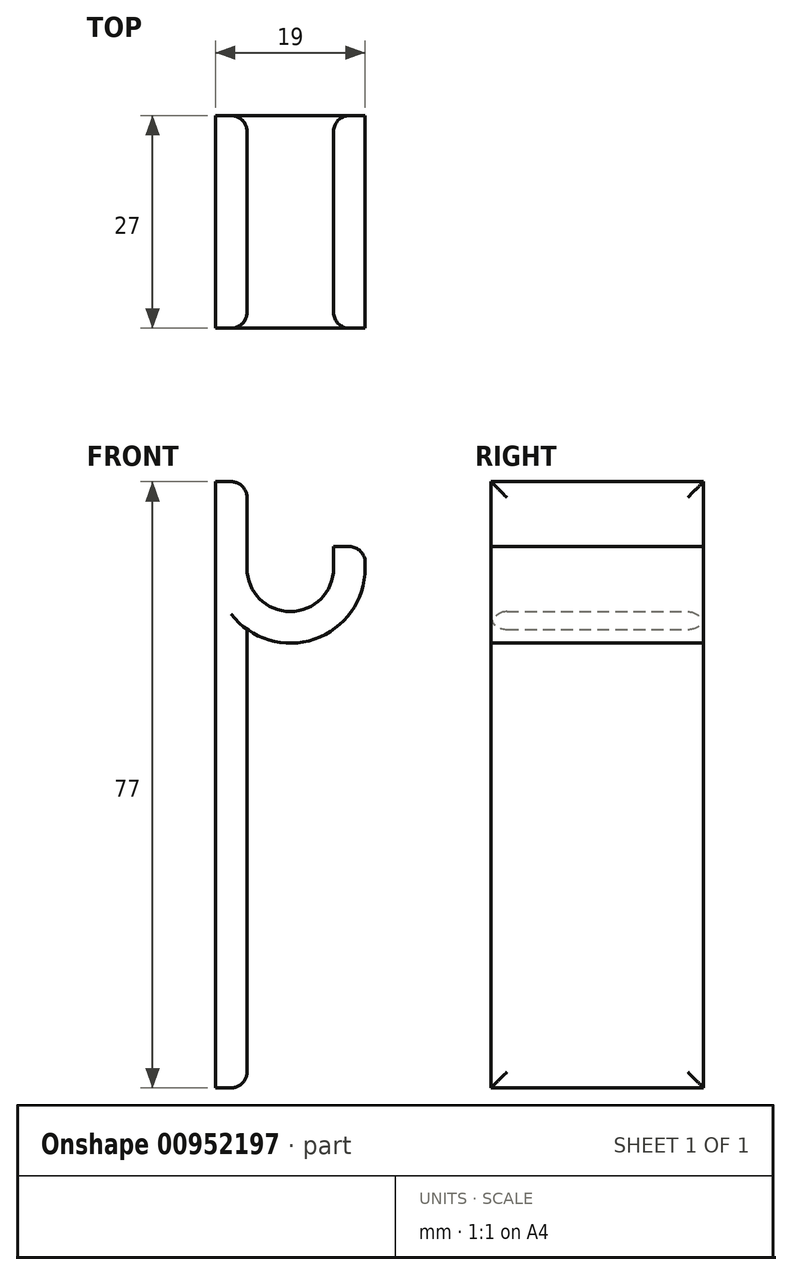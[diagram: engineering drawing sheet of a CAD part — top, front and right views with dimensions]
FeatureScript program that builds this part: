
annotation { "Feature Type Name" : "Feature", "Feature Type Description" : "" }
export const myFeature = defineFeature(function(context is Context, id is Id, definition is map)
    precondition{}
    {
        {
            assignVariable(context, id + "F0", {"name" : "stripWidth", "anyValue" : 27});
        }
        {
            var Q0;
            Q0=qCreatedBy(makeId("Front.planeOp"),FACE);
            var sketch = newSketch(context, id + "F1", { "sketchPlane" : qUnion([Q0])});
            skLineSegment(sketch, "E0.bottom", {"start": v(0, 16.5) * mm, "end": v(4, 16.5) * mm});
            skLineSegment(sketch, "E0.top", {"start": v(0, -60.5) * mm, "end": v(4, -60.5) * mm});
            skLineSegment(sketch, "E0.left", {"start": v(0, 16.5) * mm, "end": v(0, -60.5) * mm});
            skLineSegment(sketch, "E0.right", {"start": v(4, 16.5) * mm, "end": v(4, -60.5) * mm});
            skLineSegment(sketch, "E1", {"start": v(-22.13, 0) * mm, "end": v(36.5, 0) * mm});
            skArc(sketch, "E2", {"start": v(4, 5.5) * mm, "mid": v(9.5, 0) * mm, "end": v(15, 5.5) * mm});
            skArc(sketch, "E3", {"start": v(4, 13.25) * mm, "mid": v(5.14, -2.94) * mm, "end": v(19, 5.5) * mm});
            skLineSegment(sketch, "E4", {"start": v(0, 5.5) * mm, "end": v(4, 5.5) * mm});
            skLineSegment(sketch, "E5.trimOffspring", {"start": v(15, 5.5) * mm, "end": v(19, 5.5) * mm});
            skLineSegment(sketch, "E6.top", {"start": v(15, 8.25) * mm, "end": v(19, 8.25) * mm});
            skLineSegment(sketch, "E6.left", {"start": v(15, 5.5) * mm, "end": v(15, 8.25) * mm});
            skLineSegment(sketch, "E6.right", {"start": v(19, 5.5) * mm, "end": v(19, 8.25) * mm});
            skSolve(sketch);
        }
        {
            var Q0;
            Q0=qSketchRegion(id+"F1",true);
            extrude(context, id + "F2", {"entities" : qUnion([Q0]), "depth" : (getVariable(context, 'stripWidth')) * mm, "offsetDistance" : 25 * mm});
        }
        {
            var Q0;
            {var subQ0=sQuery(id+"F1.wireOp",EDGE,"E0.right");Q0=makeQuery(id+"F2.opExtrude","CAP_EDGE",EDGE,{"disambiguationData":[OSD([subQ0]),TDD([makeQuery(id+"F1.imprint","IMPRINT",EDGE,{"disambiguationData":[TD([[makeQuery(id+"F1.imprint","INTERSECT",VERTEX,{"derivedFrom":[sQuery(id+"F1.wireOp",EDGE,"E0.top"),subQ0]}),1.0]])],"derivedFrom":subQ0})])],"isStart":false});}
            var Q1;
            {var subQ0=sQuery(id+"F1.wireOp",EDGE,"E0.right");var subQ1=makeQuery(id+"F1.imprint","INTERSECT",VERTEX,{"disambiguationData":[OD(0.0)],"derivedFrom":[subQ0,sQuery(id+"F1.wireOp",EDGE,"E3")]});Q1=makeQuery(id+"F2.opExtrude","CAP_EDGE",EDGE,{"disambiguationData":[OSD([subQ0]),TDD([makeQuery(id+"F1.imprint","IMPRINT",EDGE,{"disambiguationData":[TD([[makeQuery(id+"F1.imprint","INTERSECT",VERTEX,{"derivedFrom":[sQuery(id+"F1.wireOp",EDGE,"E0.bottom"),subQ0]}),-1.0]])],"derivedFrom":subQ0}),makeQuery(id+"F1.imprint","IMPRINT",EDGE,{"disambiguationData":[TD([[subQ1,-1.0]])],"derivedFrom":subQ0})])],"isStart":false});}
            var Q2;
            {var subQ0=sQuery(id+"F1.wireOp",EDGE,"E0.right");Q2=makeQuery(id+"F2.opExtrude","CAP_EDGE",EDGE,{"disambiguationData":[OSD([subQ0]),TDD([makeQuery(id+"F1.imprint","IMPRINT",EDGE,{"disambiguationData":[TD([[makeQuery(id+"F1.imprint","INTERSECT",VERTEX,{"derivedFrom":[sQuery(id+"F1.wireOp",EDGE,"E0.top"),subQ0]}),1.0]])],"derivedFrom":subQ0})])],"isStart":true});}
            var Q3;
            Q3=makeQuery(id+"F2.opExtrude","SWEPT_EDGE",EDGE,{"disambiguationData":[OSD([sQuery(id+"F1.wireOp",EDGE,"E0.top"),sQuery(id+"F1.wireOp",EDGE,"E0.right")])]});
            var Q4;
            {var subQ0=sQuery(id+"F1.wireOp",EDGE,"E0.right");var subQ1=makeQuery(id+"F1.imprint","INTERSECT",VERTEX,{"disambiguationData":[OD(0.0)],"derivedFrom":[subQ0,sQuery(id+"F1.wireOp",EDGE,"E3")]});Q4=makeQuery(id+"F2.opExtrude","CAP_EDGE",EDGE,{"disambiguationData":[OSD([subQ0]),TDD([makeQuery(id+"F1.imprint","IMPRINT",EDGE,{"disambiguationData":[TD([[makeQuery(id+"F1.imprint","INTERSECT",VERTEX,{"derivedFrom":[sQuery(id+"F1.wireOp",EDGE,"E0.bottom"),subQ0]}),-1.0]])],"derivedFrom":subQ0}),makeQuery(id+"F1.imprint","IMPRINT",EDGE,{"disambiguationData":[TD([[subQ1,-1.0]])],"derivedFrom":subQ0})])],"isStart":true});}
            var Q5;
            Q5=makeQuery(id+"F2.opExtrude","SWEPT_EDGE",EDGE,{"disambiguationData":[OSD([sQuery(id+"F1.wireOp",EDGE,"E6.top"),sQuery(id+"F1.wireOp",EDGE,"E6.right")])]});
            var Q6;
            Q6=makeQuery(id+"F2.opExtrude","SWEPT_EDGE",EDGE,{"disambiguationData":[OSD([sQuery(id+"F1.wireOp",EDGE,"E0.bottom"),sQuery(id+"F1.wireOp",EDGE,"E0.right")])]});
            fillet(context, id + "F3", {"entities" : qUnion([Q0, Q1, Q2, Q3, Q4, Q5, Q6]), "radius" : 2 * mm, "tangentPropagation" : true, "allowEdgeOverflow" : false});
        }
    });
